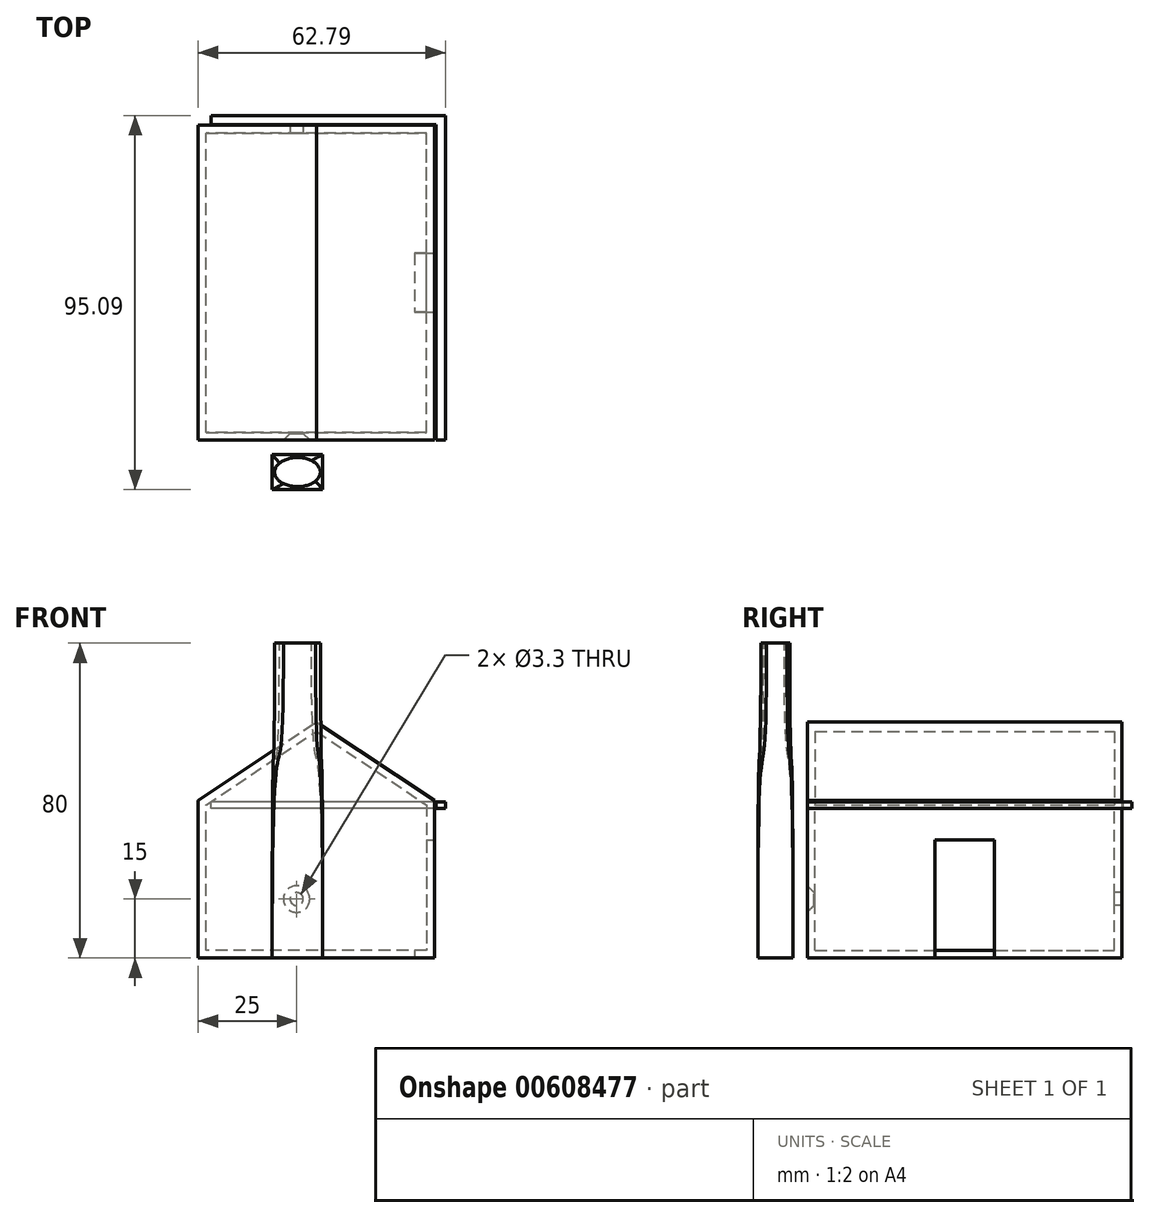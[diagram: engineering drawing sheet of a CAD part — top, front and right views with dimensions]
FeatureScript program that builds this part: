
annotation { "Feature Type Name" : "Feature", "Feature Type Description" : "" }
export const myFeature = defineFeature(function(context is Context, id is Id, definition is map)
    precondition{}
    {
        {
            var Q0;
            Q0=qCreatedBy(makeId("Front.planeOp"),FACE);
            var sketch = newSketch(context, id + "F0", { "sketchPlane" : qUnion([Q0])});
            skLineSegment(sketch, "E0", {"start": v(0, 0) * mm, "end": v(0, 40) * mm});
            skLineSegment(sketch, "E1", {"start": v(0, 40) * mm, "end": v(30, 60) * mm});
            skLineSegment(sketch, "E2", {"start": v(30, 60) * mm, "end": v(60, 40) * mm});
            skLineSegment(sketch, "E3", {"start": v(60, 40) * mm, "end": v(60, 0) * mm});
            skLineSegment(sketch, "E4", {"start": v(60, 0) * mm, "end": v(0, 0) * mm});
            skLineSegment(sketch, "E5", {"start": v(30, 60) * mm, "end": v(30, 0) * mm, "construction": true});
            skSolve(sketch);
        }
        {
            var Q0;
            Q0 = qSketchRegion(id + "F0", true);
            extrude(context, id + "F1", {"entities" : qUnion([Q0]), "depth" : 80 * mm, "offsetDistance" : 25 * mm});
        }
        {
            var Q0;
            Q0=makeQuery(id+"F1.opExtrude","SWEPT_FACE",FACE,{"disambiguationData":[OSD([sQuery(id+"F0.wireOp",EDGE,"E3")])]});
            var sketch = newSketch(context, id + "F2", { "sketchPlane" : qUnion([Q0])});
            skLineSegment(sketch, "E6.bottom", {"start": v(-47.5, 30) * mm, "end": v(-32.5, 30) * mm});
            skLineSegment(sketch, "E6.top", {"start": v(-47.5, 0) * mm, "end": v(-32.5, 0) * mm});
            skLineSegment(sketch, "E6.left", {"start": v(-47.5, 30) * mm, "end": v(-47.5, 0) * mm});
            skLineSegment(sketch, "E6.right", {"start": v(-32.5, 30) * mm, "end": v(-32.5, 0) * mm});
            skSolve(sketch);
        }
        {
            var Q0;
            Q0=makeQuery(id+"F1.opExtrude","CAP_FACE",FACE,{"disambiguationData":[OSD([sQuery(id+"F0.wireOp",EDGE,"E0"),sQuery(id+"F0.wireOp",EDGE,"E1"),sQuery(id+"F0.wireOp",EDGE,"E2"),sQuery(id+"F0.wireOp",EDGE,"E3"),sQuery(id+"F0.wireOp",EDGE,"E4")])],"isStart":false});
            var Q1;
            Q1=makeQuery(id+"F1.opExtrude","SWEPT_BODY",BODY,{"disambiguationData":[OSD([sQuery(id+"F0.wireOp",EDGE,"E0"),sQuery(id+"F0.wireOp",EDGE,"E1"),sQuery(id+"F0.wireOp",EDGE,"E2"),sQuery(id+"F0.wireOp",EDGE,"E3"),sQuery(id+"F0.wireOp",EDGE,"E4")])]});
            shell(context, id + "F3", {"isHollow" : true, "entities" : qUnion([Q0]), "parts" : qUnion([Q1]), "thickness" : 2 * mm});
        }
        {
            var Q0;
            Q0 = qSketchRegion(id + "F2", true);
            extrude(context, id + "F4", {"entities" : qUnion([Q0]), "operationType" : NewBodyOperationType.REMOVE, "oppositeDirection" : true, "depth" : 5 * mm, "offsetDistance" : 25 * mm});
        }
        {
            var Q0;
            Q0=makeQuery(id+"F1.opExtrude","CAP_FACE",FACE,{"disambiguationData":[OSD([sQuery(id+"F0.wireOp",EDGE,"E0"),sQuery(id+"F0.wireOp",EDGE,"E1"),sQuery(id+"F0.wireOp",EDGE,"E2"),sQuery(id+"F0.wireOp",EDGE,"E3"),sQuery(id+"F0.wireOp",EDGE,"E4")])],"isStart":false});
            var sketch = newSketch(context, id + "F5", { "sketchPlane" : qUnion([Q0])});
            skLineSegment(sketch, "E7", {"start": v(60, 40) * mm, "end": v(70.93, 45.48) * mm, "construction": true});
            skLineSegment(sketch, "E8", {"start": v(60, 40) * mm, "end": v(63.6, 32.83) * mm});
            skArc(sketch, "E9", {"start": v(63.6, 32.83) * mm, "mid": v(65.86, 30.09) * mm, "end": v(69.09, 28.6) * mm});
            skArc(sketch, "E10.0", {"start": v(64.5, 33.27) * mm, "mid": v(66.47, 30.88) * mm, "end": v(69.3, 29.59) * mm});
            skLineSegment(sketch, "E10.1", {"start": v(60.9, 40.45) * mm, "end": v(64.5, 33.27) * mm});
            skLineSegment(sketch, "E11", {"start": v(60.9, 40.45) * mm, "end": v(60, 40) * mm});
            skLineSegment(sketch, "E12", {"start": v(69.3, 29.59) * mm, "end": v(69.09, 28.6) * mm});
            skSolve(sketch);
        }
        {
            var Q0;
            Q0 = qSketchRegion(id + "F5", true);
            var Q1;
            Q1=sQuery(id+"F5.wireOp",EDGE,"E7");
            revolve(context, id + "F6", {"entities" : qUnion([Q0]), "axis" : qUnion([Q1]), "revolveType" : RevolveType.FULL});
        }
        {
            var Q0;
            Q0=makeQuery(id+"F1.opExtrude","CAP_FACE",FACE,{"disambiguationData":[OSD([sQuery(id+"F0.wireOp",EDGE,"E0"),sQuery(id+"F0.wireOp",EDGE,"E1"),sQuery(id+"F0.wireOp",EDGE,"E2"),sQuery(id+"F0.wireOp",EDGE,"E3"),sQuery(id+"F0.wireOp",EDGE,"E4")])],"isStart":false});
            var sketch = newSketch(context, id + "F7", { "sketchPlane" : qUnion([Q0])});
            skPoint(sketch, "E13", {"position": v(25, 15) * mm});
            skSolve(sketch);
        }
        {
            var Q0;
            Q0=sQuery(id+"F7.wireOp",VERTEX,"E13");
            var Q1;
            Q1=makeQuery(id+"F1.opExtrude","SWEPT_BODY",BODY,{"disambiguationData":[OSD([sQuery(id+"F0.wireOp",EDGE,"E0"),sQuery(id+"F0.wireOp",EDGE,"E1"),sQuery(id+"F0.wireOp",EDGE,"E2"),sQuery(id+"F0.wireOp",EDGE,"E3"),sQuery(id+"F0.wireOp",EDGE,"E4")])]});
            hole(context, id + "F8", {"style" : HoleStyle.C_SINK, "endStyle" : HoleEndStyle.THROUGH, "standardTappedOrClearance" : lookupTablePath({ "standard" : "ISO", "fit" : "Normal", "size" : "M3", "type" : "Clearance" }), "standardBlindInLast" : lookupTablePath({ "fit" : "Standard", "standard" : "ISO", "size" : "M3", "type" : "Clearance" }), "holeDiameter" : 3.3 * mm, "cSinkDiameter" : 6.72 * mm, "cSinkAngle" : 90 * degree, "majorDiameter" : 5 * mm, "isTappedThrough" : true, "tappedDepth" : 12 * mm, "tapClearance" : 3, "locations" : qUnion([Q0]), "scope" : qUnion([Q1])});
        }
        {
            var Q0;
            Q0=makeQuery(id+"F6.opRevolve","SWEPT_BODY",BODY,{"disambiguationData":[OSD([sQuery(id+"F5.wireOp",EDGE,"E8"),sQuery(id+"F5.wireOp",EDGE,"E9"),sQuery(id+"F5.wireOp",EDGE,"E10.0"),sQuery(id+"F5.wireOp",EDGE,"E10.1"),sQuery(id+"F5.wireOp",EDGE,"E11"),sQuery(id+"F5.wireOp",EDGE,"E12")])]});
            deleteBodies(context, id + "F9", {"entities" : qUnion([Q0])});
        }
        {
            var Q0;
            Q0=qCreatedBy(makeId("Top.planeOp"),FACE);
            cPlane(context, id + "F10", {"entities" : qUnion([Q0]), "cplaneType" : CPlaneType.OFFSET, "offset" : 38 * mm, "width" : 150 * mm, "height" : 150 * mm});
        }
        {
            var Q0;
            Q0=qCreatedBy(id+"F10.planeOp",FACE);
            var sketch = newSketch(context, id + "F11", { "sketchPlane" : qUnion([Q0])});
            skLineSegment(sketch, "E14", {"start": v(62.8, -80) * mm, "end": v(62.8, 2.52) * mm});
            skLineSegment(sketch, "E15", {"start": v(62.8, 2.52) * mm, "end": v(3.22, 2.52) * mm});
            skSolve(sketch);
        }
        {
            var Q0;
            Q0=makeQuery(id+"F1.opExtrude","CAP_FACE",FACE,{"disambiguationData":[OSD([sQuery(id+"F0.wireOp",EDGE,"E0"),sQuery(id+"F0.wireOp",EDGE,"E1"),sQuery(id+"F0.wireOp",EDGE,"E2"),sQuery(id+"F0.wireOp",EDGE,"E3"),sQuery(id+"F0.wireOp",EDGE,"E4")])],"isStart":false});
            var sketch = newSketch(context, id + "F12", { "sketchPlane" : qUnion([Q0])});
            skPoint(sketch, "E16.0", {"position": v(62.8, 38) * mm});
            skLineSegment(sketch, "E17.bottom", {"start": v(62.8, 38) * mm, "end": v(60.41, 38) * mm});
            skLineSegment(sketch, "E17.top", {"start": v(62.8, 39.67) * mm, "end": v(60.41, 39.67) * mm});
            skLineSegment(sketch, "E17.left", {"start": v(62.8, 38) * mm, "end": v(62.8, 39.67) * mm});
            skLineSegment(sketch, "E17.right", {"start": v(60.41, 38) * mm, "end": v(60.41, 39.67) * mm});
            skSolve(sketch);
        }
        {
            var Q0;
            Q0=makeQuery(id+"F12.imprint","IMPRINT",FACE,{"disambiguationData":[TD([[makeQuery(id+"F12.imprint","IMPRINT",EDGE,{"derivedFrom":sQuery(id+"F12.wireOp",EDGE,"E17.bottom")}),-1.0]])]});
            var Q1;
            Q1=sQuery(id+"F11.wireOp",EDGE,"E14");
            var Q2;
            Q2=sQuery(id+"F11.wireOp",EDGE,"E15");
            sweep(context, id + "F13", {"profiles" : qUnion([Q0]), "path" : qUnion([Q1, Q2])});
        }
        {
            var Q0;
            Q0=qCreatedBy(makeId("Top.planeOp"),FACE);
            var sketch = newSketch(context, id + "F14", { "sketchPlane" : qUnion([Q0])});
            skLineSegment(sketch, "E18.bottom", {"start": v(31.64, -92.57) * mm, "end": v(18.8, -92.57) * mm});
            skLineSegment(sketch, "E18.top", {"start": v(31.64, -83.6) * mm, "end": v(18.8, -83.6) * mm});
            skLineSegment(sketch, "E18.left", {"start": v(31.64, -92.57) * mm, "end": v(31.64, -83.6) * mm});
            skLineSegment(sketch, "E18.right", {"start": v(18.8, -92.57) * mm, "end": v(18.8, -83.6) * mm});
            skPoint(sketch, "E18.middle", {"position": v(25.22, -88.1) * mm});
            skSolve(sketch);
        }
        {
            var Q0;
            Q0=qCreatedBy(makeId("Top.planeOp"),FACE);
            cPlane(context, id + "F15", {"entities" : qUnion([Q0]), "cplaneType" : CPlaneType.OFFSET, "offset" : 80 * mm, "width" : 150 * mm, "height" : 150 * mm});
        }
        {
            var Q0;
            Q0=qCreatedBy(id+"F15.planeOp",FACE);
            var sketch = newSketch(context, id + "F16", { "sketchPlane" : qUnion([Q0])});
            skPoint(sketch, "E19.0", {"position": v(25.22, -88.1) * mm});
            skEllipse(sketch, "E20", {"center": v(25.22, -88.1) * mm, "majorRadius": 5.8 * mm, "minorRadius": 3.7 * mm, "majorAxis": v(1, 0)});
            skSolve(sketch);
        }
        {
            var Q0;
            Q0=makeQuery(id+"F14.imprint","IMPRINT",FACE,{"disambiguationData":[TD([[makeQuery(id+"F14.imprint","IMPRINT",EDGE,{"derivedFrom":sQuery(id+"F14.wireOp",EDGE,"E18.bottom")}),-1.0]])]});
            var Q1;
            Q1=makeQuery(id+"F16.imprint","IMPRINT",FACE,{"disambiguationData":[TD([[makeQuery(id+"F16.imprint","IMPRINT",EDGE,{"derivedFrom":sQuery(id+"F16.wireOp",EDGE,"E20")}),1.0]])]});
            loft(context, id + "F17", {"startCondition" : LoftEndDerivativeType.NORMAL_TO_PROFILE, "startMagnitude" : 3, "endCondition" : LoftEndDerivativeType.NORMAL_TO_PROFILE, "endMagnitude" : 2, "sheetProfilesArray" : [{ "sheetProfileEntities" : qUnion([Q0]) }, { "sheetProfileEntities" : qUnion([Q1]) }]});
        }
    });
